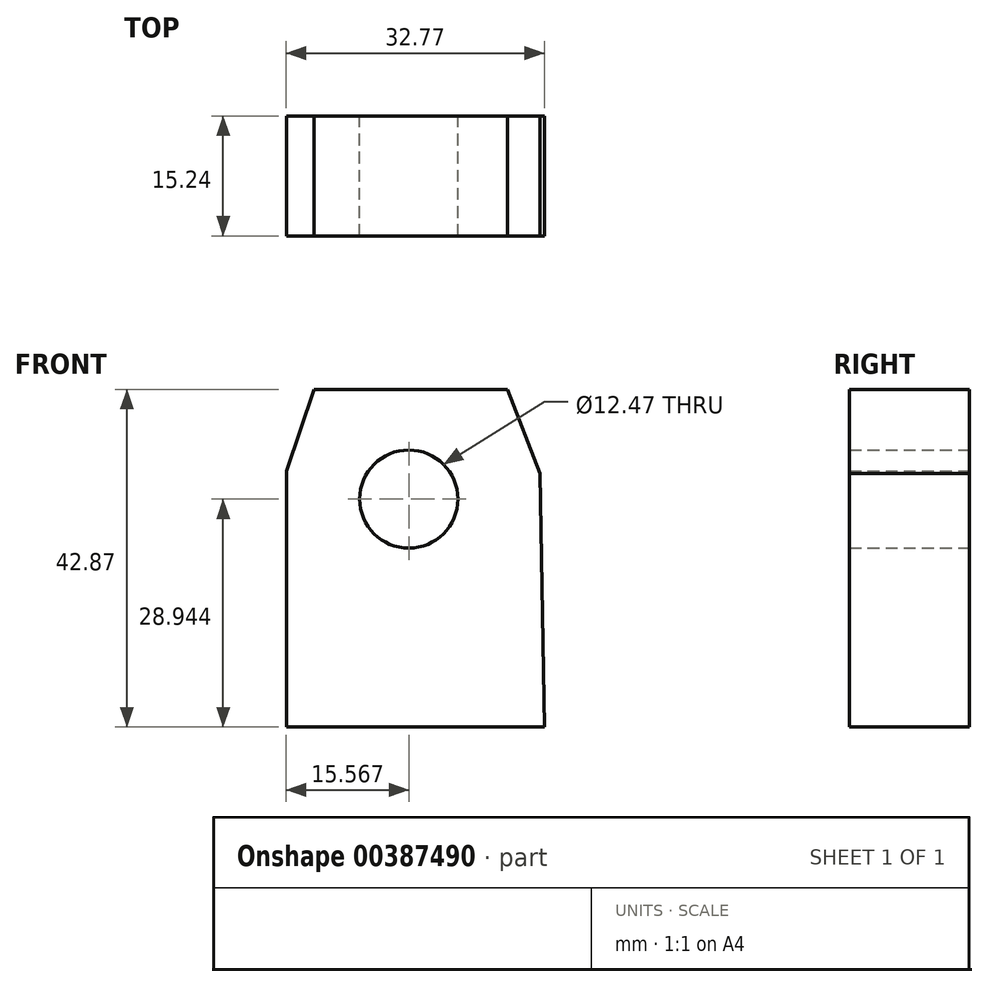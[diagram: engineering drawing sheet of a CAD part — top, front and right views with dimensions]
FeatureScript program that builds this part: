
annotation { "Feature Type Name" : "Feature", "Feature Type Description" : "" }
export const myFeature = defineFeature(function(context is Context, id is Id, definition is map)
    precondition{}
    {
        {
            var Q0;
            Q0=qCreatedBy(makeId("Front.planeOp"),FACE);
            var sketch = newSketch(context, id + "F0", { "sketchPlane" : qUnion([Q0])});
            skLineSegment(sketch, "E0", {"start": v(-19.39, 30.31) * mm, "end": v(5.19, 30.31) * mm});
            skLineSegment(sketch, "E1", {"start": v(5.19, 30.31) * mm, "end": v(9.28, 19.66) * mm});
            skLineSegment(sketch, "E2", {"start": v(-19.39, 30.31) * mm, "end": v(-22.94, 19.93) * mm});
            skPoint(sketch, "E3.end.orphan", {"position": v(11.2, -5.73) * mm});
            skPoint(sketch, "E3.start.orphan", {"position": v(-22.94, -5.73) * mm});
            skLineSegment(sketch, "E4", {"start": v(-22.94, 19.93) * mm, "end": v(-22.94, -12.56) * mm});
            skLineSegment(sketch, "E5", {"start": v(-22.94, -12.56) * mm, "end": v(9.83, -12.56) * mm});
            skLineSegment(sketch, "E6", {"start": v(9.28, 19.66) * mm, "end": v(9.83, -12.56) * mm});
            skCircle(sketch, "E7", {"center": v(-7.37, 16.38) * mm, "radius": 6.23 * mm});
            skSolve(sketch);
        }
        {
            var Q0;
            Q0=qSketchRegion(id+"F0",true);
            extrude(context, id + "F1", {"entities" : qUnion([Q0]), "depth" : 15.24 * mm});
        }
    });
